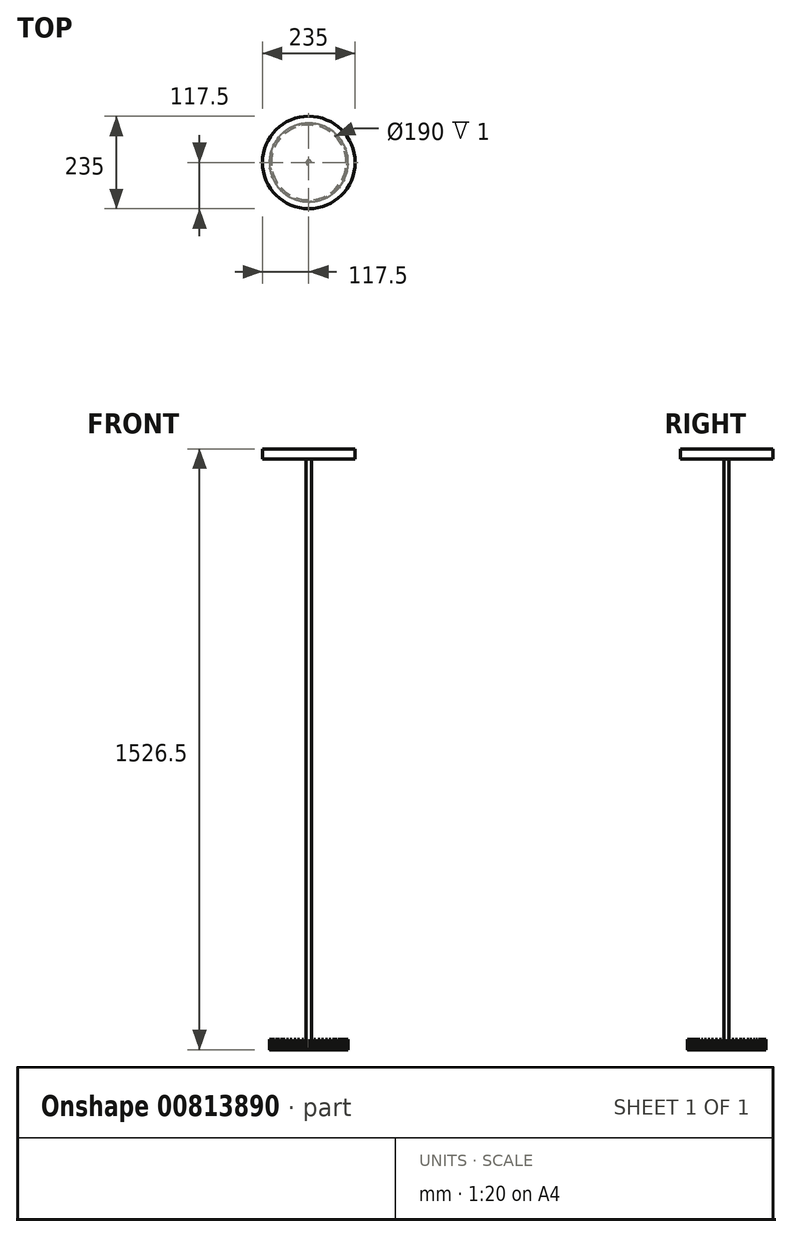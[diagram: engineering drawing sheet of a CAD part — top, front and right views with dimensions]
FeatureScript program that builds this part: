
annotation { "Feature Type Name" : "Feature", "Feature Type Description" : "" }
export const myFeature = defineFeature(function(context is Context, id is Id, definition is map)
    precondition{}
    {
        {
            var Q0;
            Q0=qCreatedBy(makeId("Top.planeOp"),FACE);
            var sketch = newSketch(context, id + "F0", { "sketchPlane" : qUnion([Q0])});
            skCircle(sketch, "E0", {"center": v(0, 0) * mm, "radius": 117.5 * mm});
            skSolve(sketch);
        }
        {
            var Q0;
            Q0 = qSketchRegion(id + "F0", true);
            extrude(context, id + "F1", {"entities" : qUnion([Q0]), "depth" : 25.4 * mm, "offsetDistance" : 25.4 * mm});
        }
        {
            var Q0;
            Q0=makeQuery(id+"F1.opExtrude","CAP_FACE",FACE,{"disambiguationData":[OSD([sQuery(id+"F0.wireOp",EDGE,"E0")])],"isStart":true});
            var sketch = newSketch(context, id + "F2", { "sketchPlane" : qUnion([Q0])});
            skCircle(sketch, "E1", {"center": v(0, 0) * mm, "radius": 6.5 * mm});
            skSolve(sketch);
        }
        {
            var Q0;
            Q0 = qSketchRegion(id + "F2", true);
            extrude(context, id + "F3", {"entities" : qUnion([Q0]), "operationType" : NewBodyOperationType.ADD, "depth" : 1500 * mm, "offsetDistance" : 25.4 * mm});
        }
        {
            var Q0;
            Q0=makeQuery(id+"F3.opExtrude","CAP_FACE",FACE,{"disambiguationData":[OSD([sQuery(id+"F2.wireOp",EDGE,"E1")])],"isStart":false});
            var sketch = newSketch(context, id + "F4", { "sketchPlane" : qUnion([Q0])});
            skCircle(sketch, "E2", {"center": v(0, 0) * mm, "radius": 100 * mm});
            skCircle(sketch, "E3", {"center": v(0, 0) * mm, "radius": 95 * mm});
            skSolve(sketch);
        }
        {
            var Q0;
            Q0 = qSketchRegion(id + "F4", true);
            extrude(context, id + "F5", {"entities" : qUnion([Q0]), "operationType" : NewBodyOperationType.ADD, "depth" : 1 * mm, "offsetDistance" : 25.4 * mm});
        }
        {
            var Q0;
            Q0=makeQuery(id+"F5.opExtrude","CAP_FACE",FACE,{"disambiguationData":[OSD([sQuery(id+"F4.wireOp",EDGE,"E2"),sQuery(id+"F4.wireOp",EDGE,"E3")])],"isStart":false});
            var sketch = newSketch(context, id + "F6", { "sketchPlane" : qUnion([Q0])});
            skCircle(sketch, "E4", {"center": v(0, 0) * mm, "radius": 95 * mm});
            skSolve(sketch);
        }
        {
            var Q0;
            Q0 = qSketchRegion(id + "F6", true);
            extrude(context, id + "F7", {"entities" : qUnion([Q0]), "depth" : 0.1 * mm, "offsetDistance" : 25.4 * mm});
        }
        {
            var Q0;
            Q0=makeQuery(id+"F5.opExtrude","CAP_FACE",FACE,{"disambiguationData":[OSD([sQuery(id+"F4.wireOp",EDGE,"E2"),sQuery(id+"F4.wireOp",EDGE,"E3")])],"isStart":true});
            var sketch = newSketch(context, id + "F8", { "sketchPlane" : qUnion([Q0])});
            skLineSegment(sketch, "E5", {"start": v(37.68, 92.63) * mm, "end": v(37.05, 90.73) * mm});
            skLineSegment(sketch, "E6", {"start": v(37.05, 90.73) * mm, "end": v(32.61, 92.2) * mm});
            skLineSegment(sketch, "E7", {"start": v(32.61, 92.2) * mm, "end": v(33.3, 94.3) * mm});
            skLineSegment(sketch, "E8", {"start": v(33.3, 94.3) * mm, "end": v(37.68, 92.63) * mm});
            skPoint(sketch, "E9.center", {"position": v(0, 0) * mm});
            skLineSegment(sketch, "E10.1.0", {"start": v(17.6, 98.44) * mm, "end": v(17.38, 96.45) * mm});
            skLineSegment(sketch, "E10.1.1", {"start": v(17.38, 96.45) * mm, "end": v(12.73, 96.97) * mm});
            skLineSegment(sketch, "E10.1.2", {"start": v(12.73, 96.97) * mm, "end": v(12.97, 99.15) * mm});
            skLineSegment(sketch, "E10.1.3", {"start": v(12.97, 99.15) * mm, "end": v(17.6, 98.44) * mm});
            skLineSegment(sketch, "E10.2.0", {"start": v(-3.25, 99.95) * mm, "end": v(-3.05, 97.96) * mm});
            skLineSegment(sketch, "E10.2.1", {"start": v(-3.05, 97.96) * mm, "end": v(-7.7, 97.5) * mm});
            skLineSegment(sketch, "E10.2.2", {"start": v(-7.7, 97.5) * mm, "end": v(-7.92, 99.69) * mm});
            skLineSegment(sketch, "E10.2.3", {"start": v(-7.92, 99.69) * mm, "end": v(-3.25, 99.95) * mm});
            skLineSegment(sketch, "E10.3.0", {"start": v(-23.96, 97.09) * mm, "end": v(-23.35, 95.18) * mm});
            skLineSegment(sketch, "E10.3.1", {"start": v(-23.35, 95.18) * mm, "end": v(-27.81, 93.76) * mm});
            skLineSegment(sketch, "E10.3.2", {"start": v(-27.81, 93.76) * mm, "end": v(-28.48, 95.86) * mm});
            skLineSegment(sketch, "E10.3.3", {"start": v(-28.48, 95.86) * mm, "end": v(-23.96, 97.09) * mm});
            skLineSegment(sketch, "E10.4.0", {"start": v(-43.62, 89.98) * mm, "end": v(-42.63, 88.25) * mm});
            skLineSegment(sketch, "E10.4.1", {"start": v(-42.63, 88.25) * mm, "end": v(-46.7, 85.93) * mm});
            skLineSegment(sketch, "E10.4.2", {"start": v(-46.7, 85.93) * mm, "end": v(-47.79, 87.84) * mm});
            skLineSegment(sketch, "E10.4.3", {"start": v(-47.79, 87.84) * mm, "end": v(-43.62, 89.98) * mm});
            skLineSegment(sketch, "E10.5.0", {"start": v(-61.38, 78.95) * mm, "end": v(-60.05, 77.45) * mm});
            skLineSegment(sketch, "E10.5.1", {"start": v(-60.05, 77.45) * mm, "end": v(-63.54, 74.35) * mm});
            skLineSegment(sketch, "E10.5.2", {"start": v(-63.54, 74.35) * mm, "end": v(-65, 75.99) * mm});
            skLineSegment(sketch, "E10.5.3", {"start": v(-65, 75.99) * mm, "end": v(-61.38, 78.95) * mm});
            skLineSegment(sketch, "E10.6.0", {"start": v(-76.45, 64.46) * mm, "end": v(-74.84, 63.28) * mm});
            skLineSegment(sketch, "E10.6.1", {"start": v(-74.84, 63.28) * mm, "end": v(-77.61, 59.5) * mm});
            skLineSegment(sketch, "E10.6.2", {"start": v(-77.61, 59.5) * mm, "end": v(-79.38, 60.81) * mm});
            skLineSegment(sketch, "E10.6.3", {"start": v(-79.38, 60.81) * mm, "end": v(-76.45, 64.46) * mm});
            skLineSegment(sketch, "E10.7.0", {"start": v(-88.18, 47.16) * mm, "end": v(-86.36, 46.33) * mm});
            skLineSegment(sketch, "E10.7.1", {"start": v(-86.36, 46.33) * mm, "end": v(-88.29, 42.07) * mm});
            skLineSegment(sketch, "E10.7.2", {"start": v(-88.29, 42.07) * mm, "end": v(-90.3, 42.98) * mm});
            skLineSegment(sketch, "E10.7.3", {"start": v(-90.3, 42.98) * mm, "end": v(-88.18, 47.16) * mm});
            skLineSegment(sketch, "E10.8.0", {"start": v(-96.06, 27.8) * mm, "end": v(-94.1, 27.36) * mm});
            skLineSegment(sketch, "E10.8.1", {"start": v(-94.1, 27.36) * mm, "end": v(-95.1, 22.8) * mm});
            skLineSegment(sketch, "E10.8.2", {"start": v(-95.1, 22.8) * mm, "end": v(-97.26, 23.27) * mm});
            skLineSegment(sketch, "E10.8.3", {"start": v(-97.26, 23.27) * mm, "end": v(-96.06, 27.8) * mm});
            skLineSegment(sketch, "E10.9.0", {"start": v(-99.74, 7.21) * mm, "end": v(-97.74, 7.2) * mm});
            skLineSegment(sketch, "E10.9.1", {"start": v(-97.74, 7.2) * mm, "end": v(-97.77, 2.52) * mm});
            skLineSegment(sketch, "E10.9.2", {"start": v(-97.77, 2.52) * mm, "end": v(-99.97, 2.54) * mm});
            skLineSegment(sketch, "E10.9.3", {"start": v(-99.97, 2.54) * mm, "end": v(-99.74, 7.21) * mm});
            skLineSegment(sketch, "E10.10.0", {"start": v(-99.06, -13.68) * mm, "end": v(-97.1, -13.28) * mm});
            skLineSegment(sketch, "E10.10.1", {"start": v(-97.1, -13.28) * mm, "end": v(-96.16, -17.86) * mm});
            skLineSegment(sketch, "E10.10.2", {"start": v(-96.16, -17.86) * mm, "end": v(-98.31, -18.3) * mm});
            skLineSegment(sketch, "E10.10.3", {"start": v(-98.31, -18.3) * mm, "end": v(-99.06, -13.68) * mm});
            skLineSegment(sketch, "E10.11.0", {"start": v(-94.05, -33.98) * mm, "end": v(-92.22, -33.18) * mm});
            skLineSegment(sketch, "E10.11.1", {"start": v(-92.22, -33.18) * mm, "end": v(-90.34, -37.46) * mm});
            skLineSegment(sketch, "E10.11.2", {"start": v(-90.34, -37.46) * mm, "end": v(-92.36, -38.34) * mm});
            skLineSegment(sketch, "E10.11.3", {"start": v(-92.36, -38.34) * mm, "end": v(-94.05, -33.98) * mm});
            skLineSegment(sketch, "E10.12.0", {"start": v(-84.93, -52.79) * mm, "end": v(-83.3, -51.62) * mm});
            skLineSegment(sketch, "E10.12.1", {"start": v(-83.3, -51.62) * mm, "end": v(-80.58, -55.42) * mm});
            skLineSegment(sketch, "E10.12.2", {"start": v(-80.58, -55.42) * mm, "end": v(-82.37, -56.7) * mm});
            skLineSegment(sketch, "E10.12.3", {"start": v(-82.37, -56.7) * mm, "end": v(-84.93, -52.79) * mm});
            skLineSegment(sketch, "E10.13.0", {"start": v(-72.1, -69.3) * mm, "end": v(-70.75, -67.82) * mm});
            skLineSegment(sketch, "E10.13.1", {"start": v(-70.75, -67.82) * mm, "end": v(-67.3, -70.97) * mm});
            skLineSegment(sketch, "E10.13.2", {"start": v(-67.3, -70.97) * mm, "end": v(-68.78, -72.6) * mm});
            skLineSegment(sketch, "E10.13.3", {"start": v(-68.78, -72.6) * mm, "end": v(-72.1, -69.3) * mm});
            skLineSegment(sketch, "E10.14.0", {"start": v(-56.12, -82.77) * mm, "end": v(-55.1, -81.04) * mm});
            skLineSegment(sketch, "E10.14.1", {"start": v(-55.1, -81.04) * mm, "end": v(-51.07, -83.4) * mm});
            skLineSegment(sketch, "E10.14.2", {"start": v(-51.07, -83.4) * mm, "end": v(-52.18, -85.3) * mm});
            skLineSegment(sketch, "E10.14.3", {"start": v(-52.18, -85.3) * mm, "end": v(-56.12, -82.77) * mm});
            skLineSegment(sketch, "E10.15.0", {"start": v(-37.68, -92.63) * mm, "end": v(-37.05, -90.73) * mm});
            skLineSegment(sketch, "E10.15.1", {"start": v(-37.05, -90.73) * mm, "end": v(-32.61, -92.2) * mm});
            skLineSegment(sketch, "E10.15.2", {"start": v(-32.61, -92.2) * mm, "end": v(-33.3, -94.3) * mm});
            skLineSegment(sketch, "E10.15.3", {"start": v(-33.3, -94.3) * mm, "end": v(-37.68, -92.63) * mm});
            skLineSegment(sketch, "E10.16.0", {"start": v(-17.6, -98.44) * mm, "end": v(-17.38, -96.45) * mm});
            skLineSegment(sketch, "E10.16.1", {"start": v(-17.38, -96.45) * mm, "end": v(-12.73, -96.97) * mm});
            skLineSegment(sketch, "E10.16.2", {"start": v(-12.73, -96.97) * mm, "end": v(-12.97, -99.15) * mm});
            skLineSegment(sketch, "E10.16.3", {"start": v(-12.97, -99.15) * mm, "end": v(-17.6, -98.44) * mm});
            skLineSegment(sketch, "E10.17.0", {"start": v(3.25, -99.95) * mm, "end": v(3.05, -97.96) * mm});
            skLineSegment(sketch, "E10.17.1", {"start": v(3.05, -97.96) * mm, "end": v(7.7, -97.5) * mm});
            skLineSegment(sketch, "E10.17.2", {"start": v(7.7, -97.5) * mm, "end": v(7.92, -99.69) * mm});
            skLineSegment(sketch, "E10.17.3", {"start": v(7.92, -99.69) * mm, "end": v(3.25, -99.95) * mm});
            skLineSegment(sketch, "E10.18.0", {"start": v(23.96, -97.09) * mm, "end": v(23.35, -95.18) * mm});
            skLineSegment(sketch, "E10.18.1", {"start": v(23.35, -95.18) * mm, "end": v(27.81, -93.76) * mm});
            skLineSegment(sketch, "E10.18.2", {"start": v(27.81, -93.76) * mm, "end": v(28.48, -95.86) * mm});
            skLineSegment(sketch, "E10.18.3", {"start": v(28.48, -95.86) * mm, "end": v(23.96, -97.09) * mm});
            skLineSegment(sketch, "E10.19.0", {"start": v(43.62, -89.98) * mm, "end": v(42.63, -88.25) * mm});
            skLineSegment(sketch, "E10.19.1", {"start": v(42.63, -88.25) * mm, "end": v(46.7, -85.93) * mm});
            skLineSegment(sketch, "E10.19.2", {"start": v(46.7, -85.93) * mm, "end": v(47.79, -87.84) * mm});
            skLineSegment(sketch, "E10.19.3", {"start": v(47.79, -87.84) * mm, "end": v(43.62, -89.98) * mm});
            skLineSegment(sketch, "E10.20.0", {"start": v(61.38, -78.95) * mm, "end": v(60.05, -77.45) * mm});
            skLineSegment(sketch, "E10.20.1", {"start": v(60.05, -77.45) * mm, "end": v(63.54, -74.35) * mm});
            skLineSegment(sketch, "E10.20.2", {"start": v(63.54, -74.35) * mm, "end": v(65, -75.99) * mm});
            skLineSegment(sketch, "E10.20.3", {"start": v(65, -75.99) * mm, "end": v(61.38, -78.95) * mm});
            skLineSegment(sketch, "E10.21.0", {"start": v(76.45, -64.46) * mm, "end": v(74.84, -63.28) * mm});
            skLineSegment(sketch, "E10.21.1", {"start": v(74.84, -63.28) * mm, "end": v(77.61, -59.5) * mm});
            skLineSegment(sketch, "E10.21.2", {"start": v(77.61, -59.5) * mm, "end": v(79.38, -60.81) * mm});
            skLineSegment(sketch, "E10.21.3", {"start": v(79.38, -60.81) * mm, "end": v(76.45, -64.46) * mm});
            skLineSegment(sketch, "E10.22.0", {"start": v(88.18, -47.16) * mm, "end": v(86.36, -46.33) * mm});
            skLineSegment(sketch, "E10.22.1", {"start": v(86.36, -46.33) * mm, "end": v(88.29, -42.07) * mm});
            skLineSegment(sketch, "E10.22.2", {"start": v(88.29, -42.07) * mm, "end": v(90.3, -42.98) * mm});
            skLineSegment(sketch, "E10.22.3", {"start": v(90.3, -42.98) * mm, "end": v(88.18, -47.16) * mm});
            skLineSegment(sketch, "E10.23.0", {"start": v(96.06, -27.8) * mm, "end": v(94.1, -27.36) * mm});
            skLineSegment(sketch, "E10.23.1", {"start": v(94.1, -27.36) * mm, "end": v(95.1, -22.8) * mm});
            skLineSegment(sketch, "E10.23.2", {"start": v(95.1, -22.8) * mm, "end": v(97.26, -23.27) * mm});
            skLineSegment(sketch, "E10.23.3", {"start": v(97.26, -23.27) * mm, "end": v(96.06, -27.8) * mm});
            skLineSegment(sketch, "E10.24.0", {"start": v(99.74, -7.21) * mm, "end": v(97.74, -7.2) * mm});
            skLineSegment(sketch, "E10.24.1", {"start": v(97.74, -7.2) * mm, "end": v(97.77, -2.52) * mm});
            skLineSegment(sketch, "E10.24.2", {"start": v(97.77, -2.52) * mm, "end": v(99.97, -2.54) * mm});
            skLineSegment(sketch, "E10.24.3", {"start": v(99.97, -2.54) * mm, "end": v(99.74, -7.21) * mm});
            skLineSegment(sketch, "E10.25.0", {"start": v(99.06, 13.68) * mm, "end": v(97.1, 13.28) * mm});
            skLineSegment(sketch, "E10.25.1", {"start": v(97.1, 13.28) * mm, "end": v(96.16, 17.86) * mm});
            skLineSegment(sketch, "E10.25.2", {"start": v(96.16, 17.86) * mm, "end": v(98.31, 18.3) * mm});
            skLineSegment(sketch, "E10.25.3", {"start": v(98.31, 18.3) * mm, "end": v(99.06, 13.68) * mm});
            skLineSegment(sketch, "E10.26.0", {"start": v(94.05, 33.98) * mm, "end": v(92.22, 33.18) * mm});
            skLineSegment(sketch, "E10.26.1", {"start": v(92.22, 33.18) * mm, "end": v(90.34, 37.46) * mm});
            skLineSegment(sketch, "E10.26.2", {"start": v(90.34, 37.46) * mm, "end": v(92.36, 38.34) * mm});
            skLineSegment(sketch, "E10.26.3", {"start": v(92.36, 38.34) * mm, "end": v(94.05, 33.98) * mm});
            skLineSegment(sketch, "E10.27.0", {"start": v(84.93, 52.79) * mm, "end": v(83.3, 51.62) * mm});
            skLineSegment(sketch, "E10.27.1", {"start": v(83.3, 51.62) * mm, "end": v(80.58, 55.42) * mm});
            skLineSegment(sketch, "E10.27.2", {"start": v(80.58, 55.42) * mm, "end": v(82.37, 56.7) * mm});
            skLineSegment(sketch, "E10.27.3", {"start": v(82.37, 56.7) * mm, "end": v(84.93, 52.79) * mm});
            skLineSegment(sketch, "E10.28.0", {"start": v(72.1, 69.3) * mm, "end": v(70.75, 67.82) * mm});
            skLineSegment(sketch, "E10.28.1", {"start": v(70.75, 67.82) * mm, "end": v(67.3, 70.97) * mm});
            skLineSegment(sketch, "E10.28.2", {"start": v(67.3, 70.97) * mm, "end": v(68.78, 72.6) * mm});
            skLineSegment(sketch, "E10.28.3", {"start": v(68.78, 72.6) * mm, "end": v(72.1, 69.3) * mm});
            skLineSegment(sketch, "E10.29.0", {"start": v(56.12, 82.77) * mm, "end": v(55.1, 81.04) * mm});
            skLineSegment(sketch, "E10.29.1", {"start": v(55.1, 81.04) * mm, "end": v(51.07, 83.4) * mm});
            skLineSegment(sketch, "E10.29.2", {"start": v(51.07, 83.4) * mm, "end": v(52.18, 85.3) * mm});
            skLineSegment(sketch, "E10.29.3", {"start": v(52.18, 85.3) * mm, "end": v(56.12, 82.77) * mm});
            skSolve(sketch);
        }
        {
            var Q0;
            Q0 = qSketchRegion(id + "F8", true);
            extrude(context, id + "F9", {"entities" : qUnion([Q0]), "operationType" : NewBodyOperationType.ADD, "depth" : 25.4 * mm, "offsetDistance" : 25.4 * mm});
        }
    });
